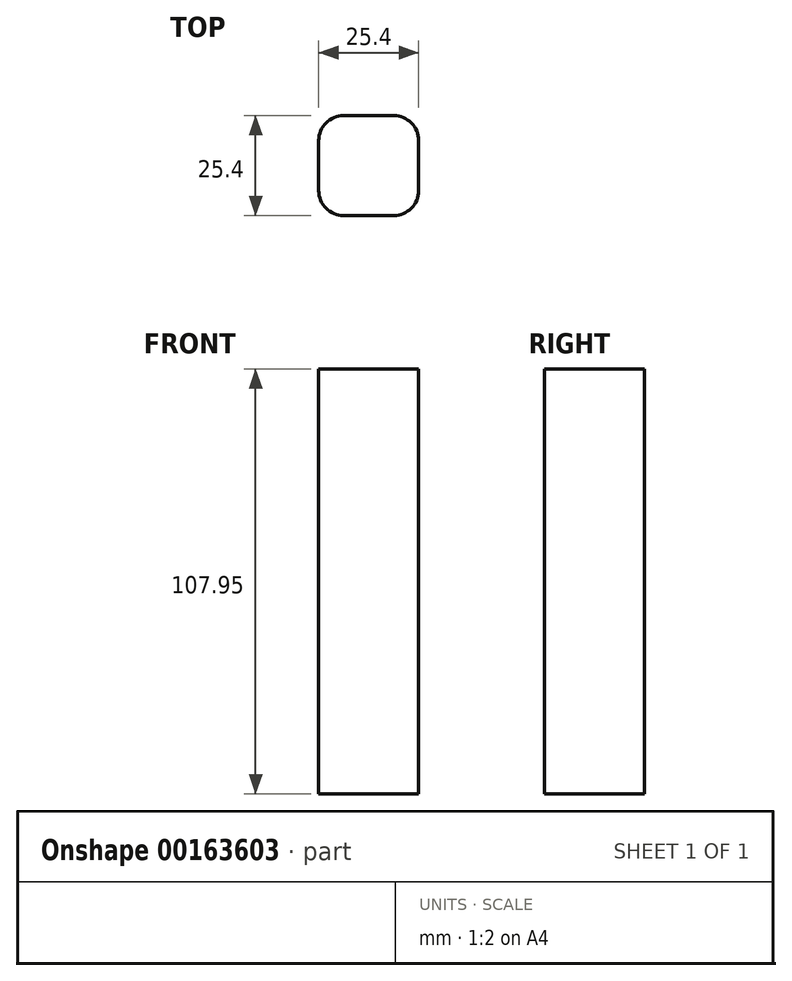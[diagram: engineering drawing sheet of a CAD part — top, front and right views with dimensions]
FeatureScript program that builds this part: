
annotation { "Feature Type Name" : "Feature", "Feature Type Description" : "" }
export const myFeature = defineFeature(function(context is Context, id is Id, definition is map)
    precondition{}
    {
        {
            var Q0;
            Q0=qCreatedBy(makeId("Top.planeOp"),FACE);
            var sketch = newSketch(context, id + "F0", { "sketchPlane" : qUnion([Q0])});
            skLineSegment(sketch, "E0.bottom", {"start": v(6.35, 12.7) * mm, "end": v(-6.35, 12.7) * mm});
            skLineSegment(sketch, "E0.top", {"start": v(6.35, -12.7) * mm, "end": v(-6.35, -12.7) * mm});
            skLineSegment(sketch, "E0.left", {"start": v(12.7, 6.35) * mm, "end": v(12.7, -6.35) * mm});
            skLineSegment(sketch, "E0.right", {"start": v(-12.7, 6.35) * mm, "end": v(-12.7, -6.35) * mm});
            skPoint(sketch, "E0.middle", {"position": v(0, 0) * mm});
            skPoint(sketch, "E1.visualSharp", {"position": v(-12.7, 12.7) * mm});
            skArc(sketch, "E1.filletArc", {"start": v(-6.35, 12.7) * mm, "mid": v(-10.84, 10.84) * mm, "end": v(-12.7, 6.35) * mm});
            skPoint(sketch, "E2.visualSharp", {"position": v(12.7, 12.7) * mm});
            skArc(sketch, "E2.filletArc", {"start": v(12.7, 6.35) * mm, "mid": v(10.84, 10.84) * mm, "end": v(6.35, 12.7) * mm});
            skPoint(sketch, "E3.visualSharp", {"position": v(12.7, -12.7) * mm});
            skArc(sketch, "E3.filletArc", {"start": v(6.35, -12.7) * mm, "mid": v(10.84, -10.84) * mm, "end": v(12.7, -6.35) * mm});
            skPoint(sketch, "E4.visualSharp", {"position": v(-12.7, -12.7) * mm});
            skArc(sketch, "E4.filletArc", {"start": v(-12.7, -6.35) * mm, "mid": v(-10.84, -10.84) * mm, "end": v(-6.35, -12.7) * mm});
            skSolve(sketch);
        }
        {
            var Q0;
            Q0 = qSketchRegion(id + "F0", true);
            extrude(context, id + "F1", {"entities" : qUnion([Q0]), "depth" : 107.95 * mm});
        }
    });
